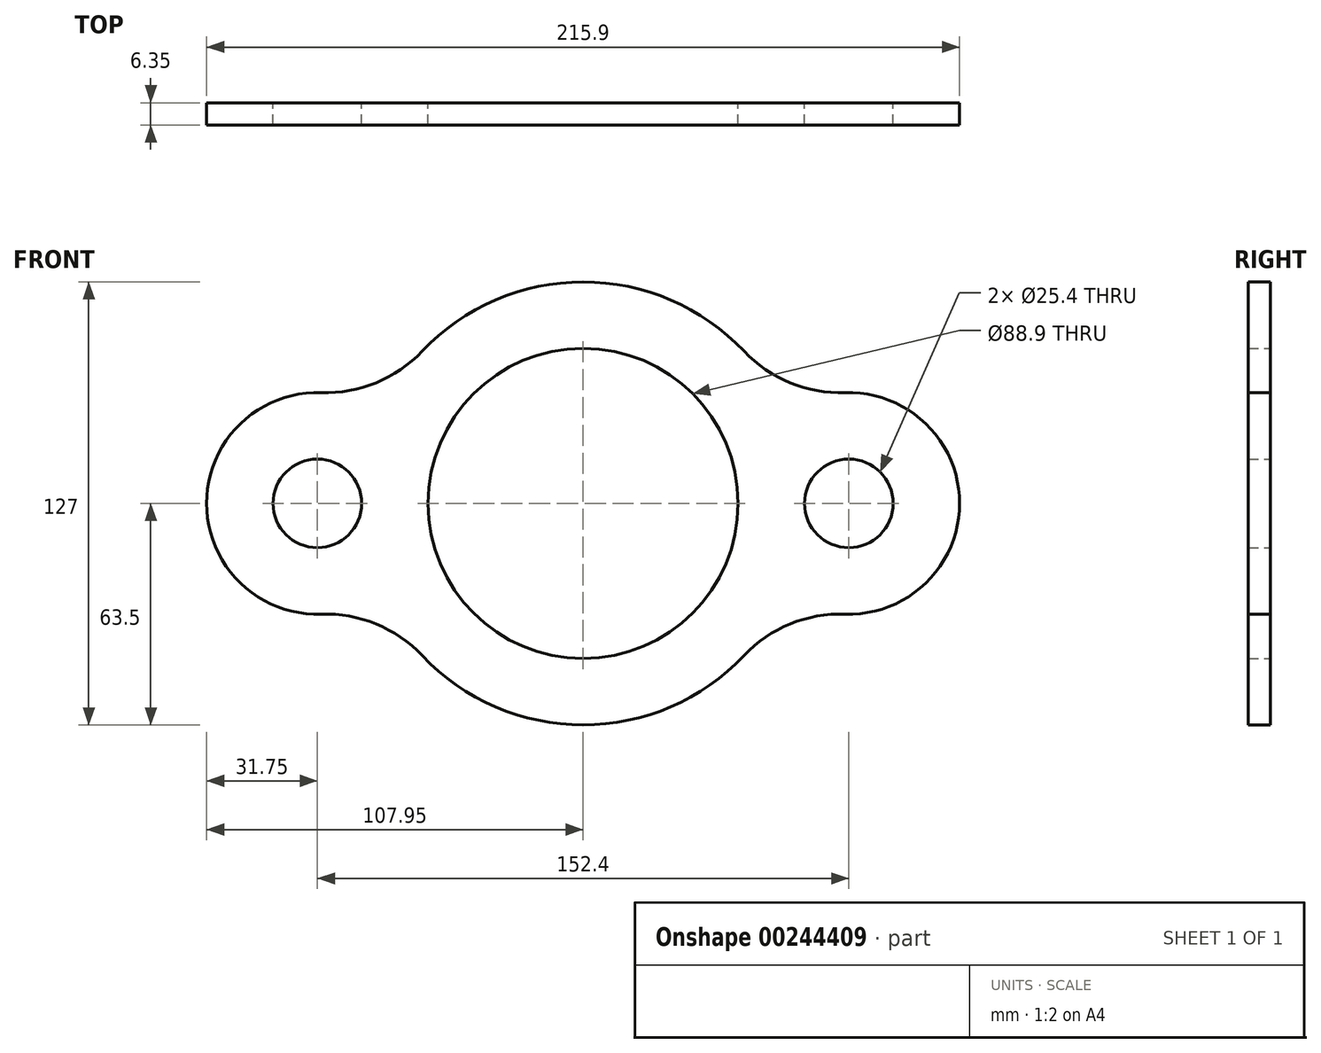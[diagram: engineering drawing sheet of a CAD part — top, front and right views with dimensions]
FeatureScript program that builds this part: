
annotation { "Feature Type Name" : "Feature", "Feature Type Description" : "" }
export const myFeature = defineFeature(function(context is Context, id is Id, definition is map)
    precondition{}
    {
        {
            var Q0;
            Q0=qCreatedBy(makeId("Front.planeOp"),FACE);
            var sketch = newSketch(context, id + "F0", { "sketchPlane" : qUnion([Q0])});
            skArc(sketch, "E0", {"start": v(-46.14, -43.63) * mm, "mid": v(0, -63.5) * mm, "end": v(46.14, -43.63) * mm});
            skCircle(sketch, "E1", {"center": v(0, 0) * mm, "radius": 44.45 * mm});
            skCircle(sketch, "E2", {"center": v(76.2, 0) * mm, "radius": 12.7 * mm});
            skArc(sketch, "E3", {"start": v(75.12, -31.73) * mm, "mid": v(107.95, 0) * mm, "end": v(75.12, 31.73) * mm});
            skCircle(sketch, "E4", {"center": v(-76.2, 0) * mm, "radius": 12.7 * mm});
            skArc(sketch, "E5", {"start": v(-75.12, 31.73) * mm, "mid": v(-107.95, 0) * mm, "end": v(-75.12, -31.73) * mm});
            skArc(sketch, "E6.trimOffspring", {"start": v(46.14, 43.63) * mm, "mid": v(0, 63.5) * mm, "end": v(-46.14, 43.63) * mm});
            skPoint(sketch, "E7.visualSharp", {"position": v(-57.94, 25.98) * mm});
            skArc(sketch, "E7.filletArc", {"start": v(-75.12, 31.73) * mm, "mid": v(-59.35, 34.56) * mm, "end": v(-46.14, 43.63) * mm});
            skPoint(sketch, "E8.visualSharp", {"position": v(-57.94, -25.98) * mm});
            skArc(sketch, "E8.filletArc", {"start": v(-46.14, -43.63) * mm, "mid": v(-59.35, -34.56) * mm, "end": v(-75.12, -31.73) * mm});
            skPoint(sketch, "E9.visualSharp", {"position": v(57.94, -25.98) * mm});
            skArc(sketch, "E9.filletArc", {"start": v(75.12, -31.73) * mm, "mid": v(59.35, -34.56) * mm, "end": v(46.14, -43.63) * mm});
            skPoint(sketch, "E10.visualSharp", {"position": v(57.94, 25.98) * mm});
            skArc(sketch, "E10.filletArc", {"start": v(46.14, 43.63) * mm, "mid": v(59.35, 34.56) * mm, "end": v(75.12, 31.73) * mm});
            skSolve(sketch);
        }
        {
            var Q0;
            Q0=makeQuery(id+"F0.imprint","IMPRINT",FACE,{"disambiguationData":[TD([[makeQuery(id+"F0.imprint","IMPRINT",EDGE,{"derivedFrom":sQuery(id+"F0.wireOp",EDGE,"E0")}),1.0]])]});
            extrude(context, id + "F1", {"entities" : qUnion([Q0]), "depth" : 6.35 * mm});
        }
    });
